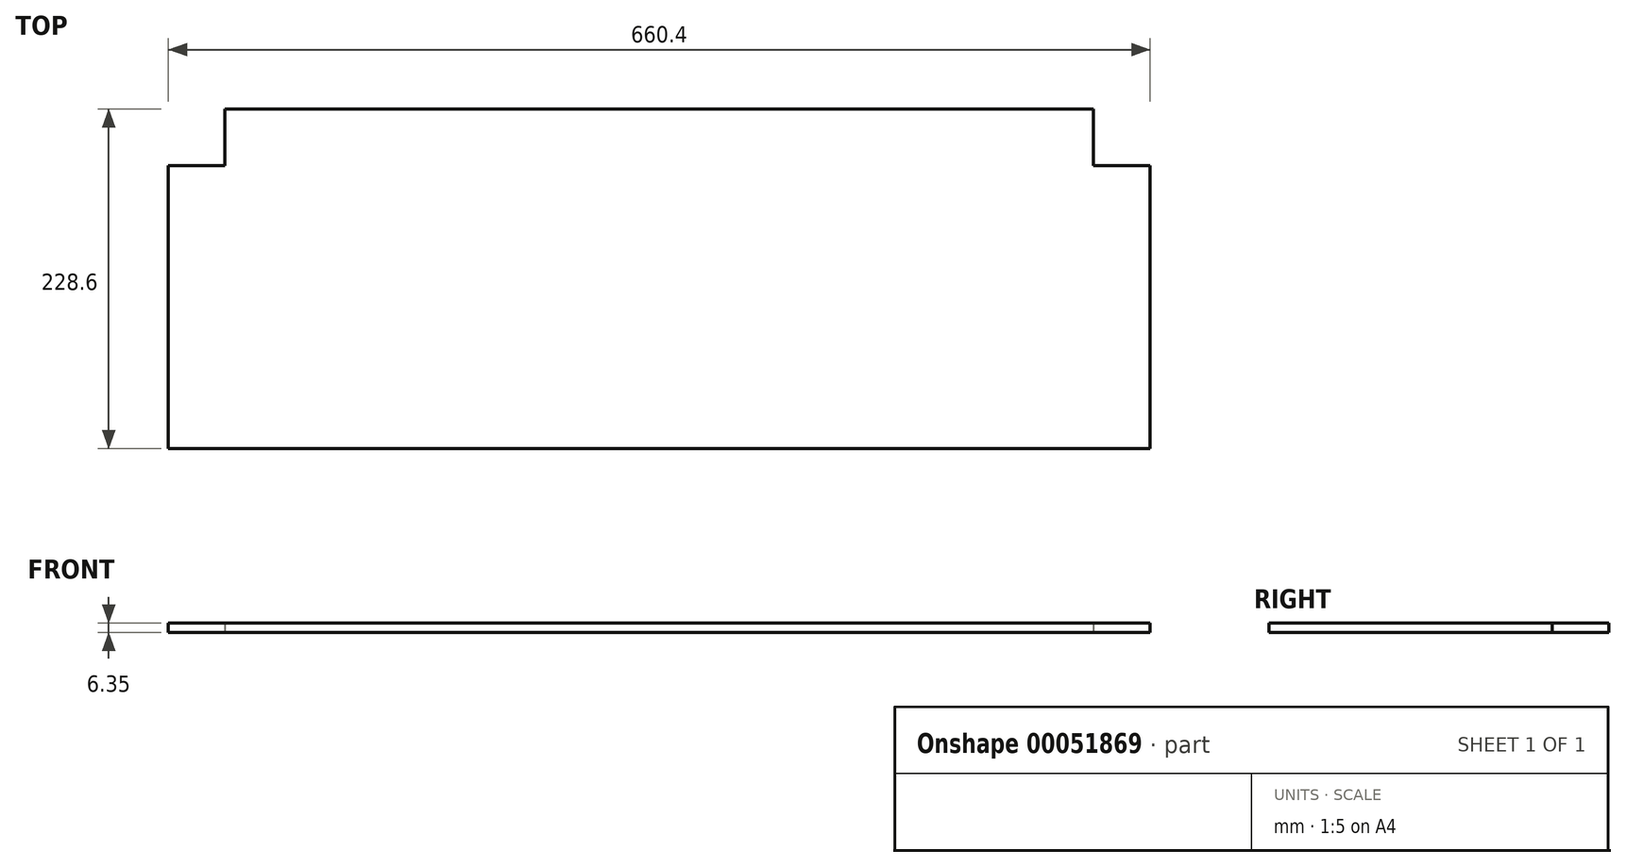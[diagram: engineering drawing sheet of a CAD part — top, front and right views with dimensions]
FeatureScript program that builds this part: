
annotation { "Feature Type Name" : "Feature", "Feature Type Description" : "" }
export const myFeature = defineFeature(function(context is Context, id is Id, definition is map)
    precondition{}
    {
        {
            var Q0;
            Q0=qCreatedBy(makeId("Top.planeOp"),FACE);
            var sketch = newSketch(context, id + "F0", { "sketchPlane" : qUnion([Q0])});
            skLineSegment(sketch, "E0", {"start": v(-330.2, -101.6) * mm, "end": v(-330.2, 88.9) * mm});
            skLineSegment(sketch, "E1", {"start": v(-330.2, 88.9) * mm, "end": v(-292.1, 88.9) * mm});
            skLineSegment(sketch, "E2", {"start": v(-292.1, 88.9) * mm, "end": v(-292.1, 127) * mm});
            skLineSegment(sketch, "E3", {"start": v(-292.1, 127) * mm, "end": v(292.1, 127) * mm});
            skLineSegment(sketch, "E4", {"start": v(292.1, 127) * mm, "end": v(292.1, 88.9) * mm});
            skLineSegment(sketch, "E5", {"start": v(292.1, 88.9) * mm, "end": v(330.2, 88.9) * mm});
            skLineSegment(sketch, "E6", {"start": v(330.2, 88.9) * mm, "end": v(330.2, -101.6) * mm});
            skLineSegment(sketch, "E7", {"start": v(330.2, -101.6) * mm, "end": v(-330.2, -101.6) * mm});
            skSolve(sketch);
        }
        {
            var Q0;
            Q0=makeQuery(id+"F0.imprint","IMPRINT",FACE,{"disambiguationData":[TD([[makeQuery(id+"F0.imprint","IMPRINT",EDGE,{"derivedFrom":sQuery(id+"F0.wireOp",EDGE,"E0")}),-1.0]])]});
            extrude(context, id + "F1", {"entities" : qUnion([Q0]), "depth" : 6.35 * mm});
        }
    });
